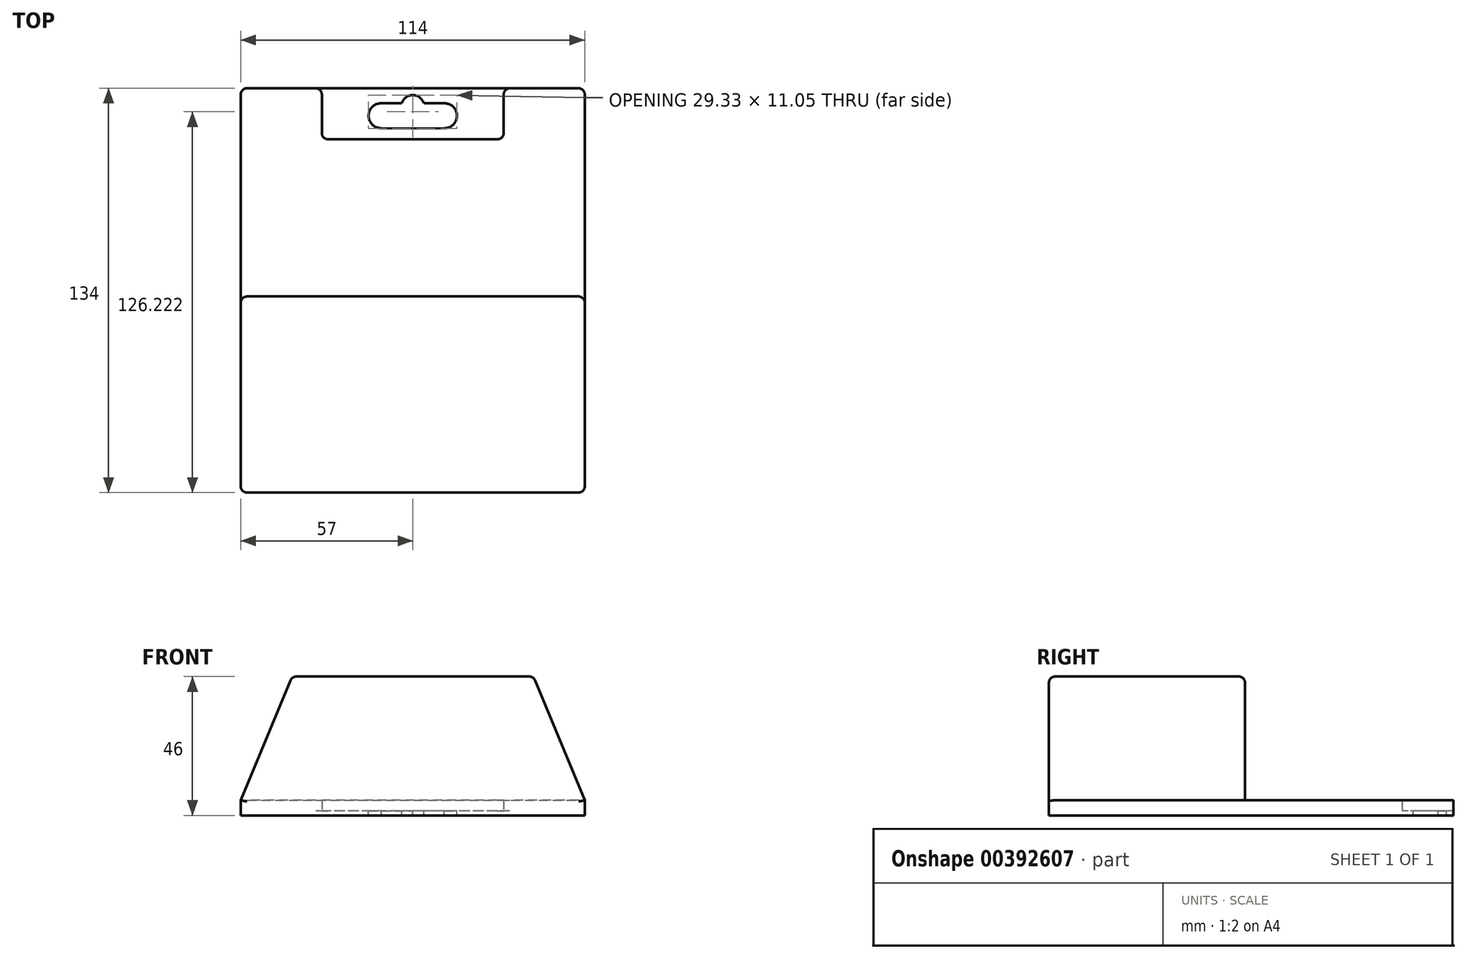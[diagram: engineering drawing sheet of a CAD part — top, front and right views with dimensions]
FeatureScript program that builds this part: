
annotation { "Feature Type Name" : "Feature", "Feature Type Description" : "" }
export const myFeature = defineFeature(function(context is Context, id is Id, definition is map)
    precondition{}
    {
        {
            var Q0;
            Q0=qCreatedBy(makeId("Front.planeOp"),FACE);
            var sketch = newSketch(context, id + "F0", { "sketchPlane" : qUnion([Q0])});
            skLineSegment(sketch, "E0", {"start": v(0, 46) * mm, "end": v(-40, 46) * mm});
            skLineSegment(sketch, "E1", {"start": v(-40, 46) * mm, "end": v(-57, 5) * mm});
            skLineSegment(sketch, "E2", {"start": v(-57, 5) * mm, "end": v(0, 5) * mm});
            skLineSegment(sketch, "E3.MirrorCS", {"start": v(0, 46) * mm, "end": v(40, 46) * mm});
            skLineSegment(sketch, "E4.MirrorCS", {"start": v(40, 46) * mm, "end": v(57, 5) * mm});
            skLineSegment(sketch, "E5.MirrorCS", {"start": v(57, 5) * mm, "end": v(0, 5) * mm});
            skSolve(sketch);
        }
        {
            var Q0;
            Q0 = qSketchRegion(id + "F0", true);
            extrude(context, id + "F1", {"entities" : qUnion([Q0]), "depth" : 65 * mm});
        }
        {
            var Q0;
            Q0=qCreatedBy(makeId("Front.planeOp"),FACE);
            var sketch = newSketch(context, id + "F2", { "sketchPlane" : qUnion([Q0])});
            skLineSegment(sketch, "E6.bottom", {"start": v(0, 0) * mm, "end": v(-57, 0) * mm});
            skLineSegment(sketch, "E6.top", {"start": v(0, 5) * mm, "end": v(-57, 5) * mm});
            skLineSegment(sketch, "E6.left", {"start": v(0, 0) * mm, "end": v(0, 5) * mm});
            skLineSegment(sketch, "E6.right", {"start": v(-57, 0) * mm, "end": v(-57, 5) * mm});
            skLineSegment(sketch, "E7.MirrorCS", {"start": v(0, 5) * mm, "end": v(57, 5) * mm});
            skLineSegment(sketch, "E8.MirrorCS", {"start": v(57, 0) * mm, "end": v(57, 5) * mm});
            skLineSegment(sketch, "E9.MirrorCS", {"start": v(0, 0) * mm, "end": v(57, 0) * mm});
            skSolve(sketch);
        }
        {
            var Q0;
            Q0 = qSketchRegion(id + "F2", true);
            var Q1;
            Q1=makeQuery(id+"F1.opExtrude","CAP_FACE",FACE,{"disambiguationData":[OSD([sQuery(id+"F0.wireOp",EDGE,"E0"),sQuery(id+"F0.wireOp",EDGE,"E1"),sQuery(id+"F0.wireOp",EDGE,"E2"),sQuery(id+"F0.wireOp",EDGE,"E3.MirrorCS"),sQuery(id+"F0.wireOp",EDGE,"E4.MirrorCS"),sQuery(id+"F0.wireOp",EDGE,"E5.MirrorCS")])],"isStart":false});
            extrude(context, id + "F3", {"entities" : qUnion([Q0]), "operationType" : NewBodyOperationType.ADD, "endBound" : BoundingType.UP_TO_SURFACE, "endBoundEntityFace" : qUnion([Q1]), "depth" : 160 * mm, "hasSecondDirection" : true, "secondDirectionOppositeDirection" : true, "secondDirectionDepth" : 69 * mm});
        }
        {
            var Q0;
            Q0=qCreatedBy(makeId("Top.planeOp"),FACE);
            cPlane(context, id + "F4", {"entities" : qUnion([Q0]), "cplaneType" : CPlaneType.OFFSET, "offset" : 5 * mm, "width" : 150 * mm, "height" : 150 * mm});
        }
        {
            var Q0;
            Q0=qCreatedBy(id+"F4.planeOp",FACE);
            var sketch = newSketch(context, id + "F5", { "sketchPlane" : qUnion([Q0])});
            skLineSegment(sketch, "E10.bottom", {"start": v(0, 69.9) * mm, "end": v(30.15, 69.9) * mm});
            skLineSegment(sketch, "E10.top", {"start": v(0, 52.12) * mm, "end": v(30.15, 52.12) * mm});
            skLineSegment(sketch, "E10.right", {"start": v(30.15, 69.9) * mm, "end": v(30.15, 52.12) * mm});
            skLineSegment(sketch, "E11.MirrorCS", {"start": v(0, 52.12) * mm, "end": v(-30.15, 52.12) * mm});
            skLineSegment(sketch, "E12.MirrorCS", {"start": v(-30.15, 69.9) * mm, "end": v(-30.15, 52.12) * mm});
            skLineSegment(sketch, "E13.MirrorCS", {"start": v(0, 69.9) * mm, "end": v(-30.15, 69.9) * mm});
            skSolve(sketch);
        }
        {
            var Q0;
            Q0 = qSketchRegion(id + "F5", true);
            extrude(context, id + "F6", {"entities" : qUnion([Q0]), "operationType" : NewBodyOperationType.REMOVE, "oppositeDirection" : true, "depth" : 3.5 * mm});
        }
        {
            var Q0;
            Q0=qCreatedBy(id+"F4.planeOp",FACE);
            var sketch = newSketch(context, id + "F7", { "sketchPlane" : qUnion([Q0])});
            skArc(sketch, "E14", {"start": v(-10.4, 64) * mm, "mid": v(-14.66, 59.98) * mm, "end": v(-10.58, 55.77) * mm});
            skArc(sketch, "E15", {"start": v(0, 66.75) * mm, "mid": v(-2.28, 65.98) * mm, "end": v(-3.64, 64) * mm});
            skLineSegment(sketch, "E16", {"start": v(-10.58, 55.77) * mm, "end": v(0, 55.7) * mm});
            skLineSegment(sketch, "E17", {"start": v(-10.4, 64) * mm, "end": v(-3.64, 64) * mm});
            skLineSegment(sketch, "E18.MirrorCS", {"start": v(10.58, 55.77) * mm, "end": v(0, 55.7) * mm});
            skArc(sketch, "E19.MirrorCS", {"start": v(10.4, 64) * mm, "mid": v(14.66, 59.98) * mm, "end": v(10.58, 55.77) * mm});
            skLineSegment(sketch, "E20.MirrorCS", {"start": v(10.4, 64) * mm, "end": v(3.64, 64) * mm});
            skArc(sketch, "E21.MirrorCS", {"start": v(0, 66.75) * mm, "mid": v(2.28, 65.98) * mm, "end": v(3.64, 64) * mm});
            skSolve(sketch);
        }
        {
            var Q0;
            Q0 = qSketchRegion(id + "F7", true);
            extrude(context, id + "F8", {"entities" : qUnion([Q0]), "operationType" : NewBodyOperationType.REMOVE, "endBound" : BoundingType.SYMMETRIC, "oppositeDirection" : true, "depth" : 25 * mm});
        }
        {
            var Q0;
            Q0=makeQuery(id+"F1.opExtrude","SWEPT_EDGE",EDGE,{"disambiguationData":[OSD([sQuery(id+"F0.wireOp",EDGE,"E3.MirrorCS"),sQuery(id+"F0.wireOp",EDGE,"E4.MirrorCS")])]});
            var Q1;
            Q1=makeQuery(id+"F1.opExtrude","SWEPT_EDGE",EDGE,{"disambiguationData":[OSD([sQuery(id+"F0.wireOp",EDGE,"E0"),sQuery(id+"F0.wireOp",EDGE,"E1")])]});
            var Q2;
            Q2=makeQuery(id+"F1.opExtrude","CAP_EDGE",EDGE,{"disambiguationData":[OSD([sQuery(id+"F0.wireOp",EDGE,"E0"),sQuery(id+"F0.wireOp",EDGE,"E3.MirrorCS")])],"isStart":true});
            var Q3;
            Q3=makeQuery(id+"F1.opExtrude","CAP_EDGE",EDGE,{"disambiguationData":[OSD([sQuery(id+"F0.wireOp",EDGE,"E1")])],"isStart":true});
            var Q4;
            Q4=makeQuery(id+"F1.opExtrude","CAP_EDGE",EDGE,{"disambiguationData":[OSD([sQuery(id+"F0.wireOp",EDGE,"E4.MirrorCS")])],"isStart":true});
            var Q5;
            Q5=makeQuery(id+"F1.opExtrude","CAP_EDGE",EDGE,{"disambiguationData":[OSD([sQuery(id+"F0.wireOp",EDGE,"E4.MirrorCS")])],"isStart":false});
            var Q6;
            Q6=makeQuery(id+"F1.opExtrude","CAP_EDGE",EDGE,{"disambiguationData":[OSD([sQuery(id+"F0.wireOp",EDGE,"E0"),sQuery(id+"F0.wireOp",EDGE,"E3.MirrorCS")])],"isStart":false});
            var Q7;
            Q7=makeQuery(id+"F1.opExtrude","CAP_EDGE",EDGE,{"disambiguationData":[OSD([sQuery(id+"F0.wireOp",EDGE,"E1")])],"isStart":false});
            var Q8;
            Q8=makeQuery(id+"F6.boolean.opBoolean","COPY",EDGE,{"derivedFrom":makeQuery(id+"F6.opExtrude","SWEPT_EDGE",EDGE,{"disambiguationData":[OSD([sQuery(id+"F5.wireOp",EDGE,"E10.top"),sQuery(id+"F5.wireOp",EDGE,"E10.right")])]})});
            var Q9;
            Q9=makeQuery(id+"F6.boolean.opBoolean","COPY",EDGE,{"derivedFrom":makeQuery(id+"F6.opExtrude","SWEPT_EDGE",EDGE,{"disambiguationData":[OSD([sQuery(id+"F5.wireOp",EDGE,"E11.MirrorCS"),sQuery(id+"F5.wireOp",EDGE,"E12.MirrorCS")])]})});
            var Q10;
            Q10=makeQuery(id+"F6.boolean.opBoolean","INTERSECT",EDGE,{"derivedFrom":[makeQuery(id+"F3.opExtrude","CAP_FACE",FACE,{"disambiguationData":[OSD([sQuery(id+"F2.wireOp",EDGE,"E6.bottom"),sQuery(id+"F2.wireOp",EDGE,"E6.top"),sQuery(id+"F2.wireOp",EDGE,"E6.right"),sQuery(id+"F2.wireOp",EDGE,"E7.MirrorCS"),sQuery(id+"F2.wireOp",EDGE,"E8.MirrorCS"),sQuery(id+"F2.wireOp",EDGE,"E9.MirrorCS")])],"isStart":true}),makeQuery(id+"F6.opExtrude","SWEPT_FACE",FACE,{"disambiguationData":[OSD([sQuery(id+"F5.wireOp",EDGE,"E10.right")])]})]});
            var Q11;
            Q11=makeQuery(id+"F6.boolean.opBoolean","INTERSECT",EDGE,{"derivedFrom":[makeQuery(id+"F3.opExtrude","CAP_FACE",FACE,{"disambiguationData":[OSD([sQuery(id+"F2.wireOp",EDGE,"E6.bottom"),sQuery(id+"F2.wireOp",EDGE,"E6.top"),sQuery(id+"F2.wireOp",EDGE,"E6.right"),sQuery(id+"F2.wireOp",EDGE,"E7.MirrorCS"),sQuery(id+"F2.wireOp",EDGE,"E8.MirrorCS"),sQuery(id+"F2.wireOp",EDGE,"E9.MirrorCS")])],"isStart":true}),makeQuery(id+"F6.opExtrude","SWEPT_FACE",FACE,{"disambiguationData":[OSD([sQuery(id+"F5.wireOp",EDGE,"E12.MirrorCS")])]})]});
            var Q12;
            Q12=makeQuery(id+"F3.opExtrude","CAP_EDGE",EDGE,{"disambiguationData":[OSD([sQuery(id+"F2.wireOp",EDGE,"E6.right")])],"isStart":true});
            var Q13;
            Q13=makeQuery(id+"F3.opExtrude","CAP_EDGE",EDGE,{"disambiguationData":[OSD([sQuery(id+"F2.wireOp",EDGE,"E8.MirrorCS")])],"isStart":true});
            var Q14;
            Q14=makeQuery(id+"F3.opExtrude","CAP_EDGE",EDGE,{"disambiguationData":[OSD([sQuery(id+"F2.wireOp",EDGE,"E6.right")])],"isStart":false});
            var Q15;
            Q15=makeQuery(id+"F3.opExtrude","CAP_EDGE",EDGE,{"disambiguationData":[OSD([sQuery(id+"F2.wireOp",EDGE,"E8.MirrorCS")])],"isStart":false});
            fillet(context, id + "F9", {"entities" : qUnion([Q0, Q1, Q2, Q3, Q4, Q5, Q6, Q7, Q8, Q9, Q10, Q11, Q12, Q13, Q14, Q15]), "radius" : 2 * mm, "tangentPropagation" : true, "allowEdgeOverflow" : false});
        }
    });
